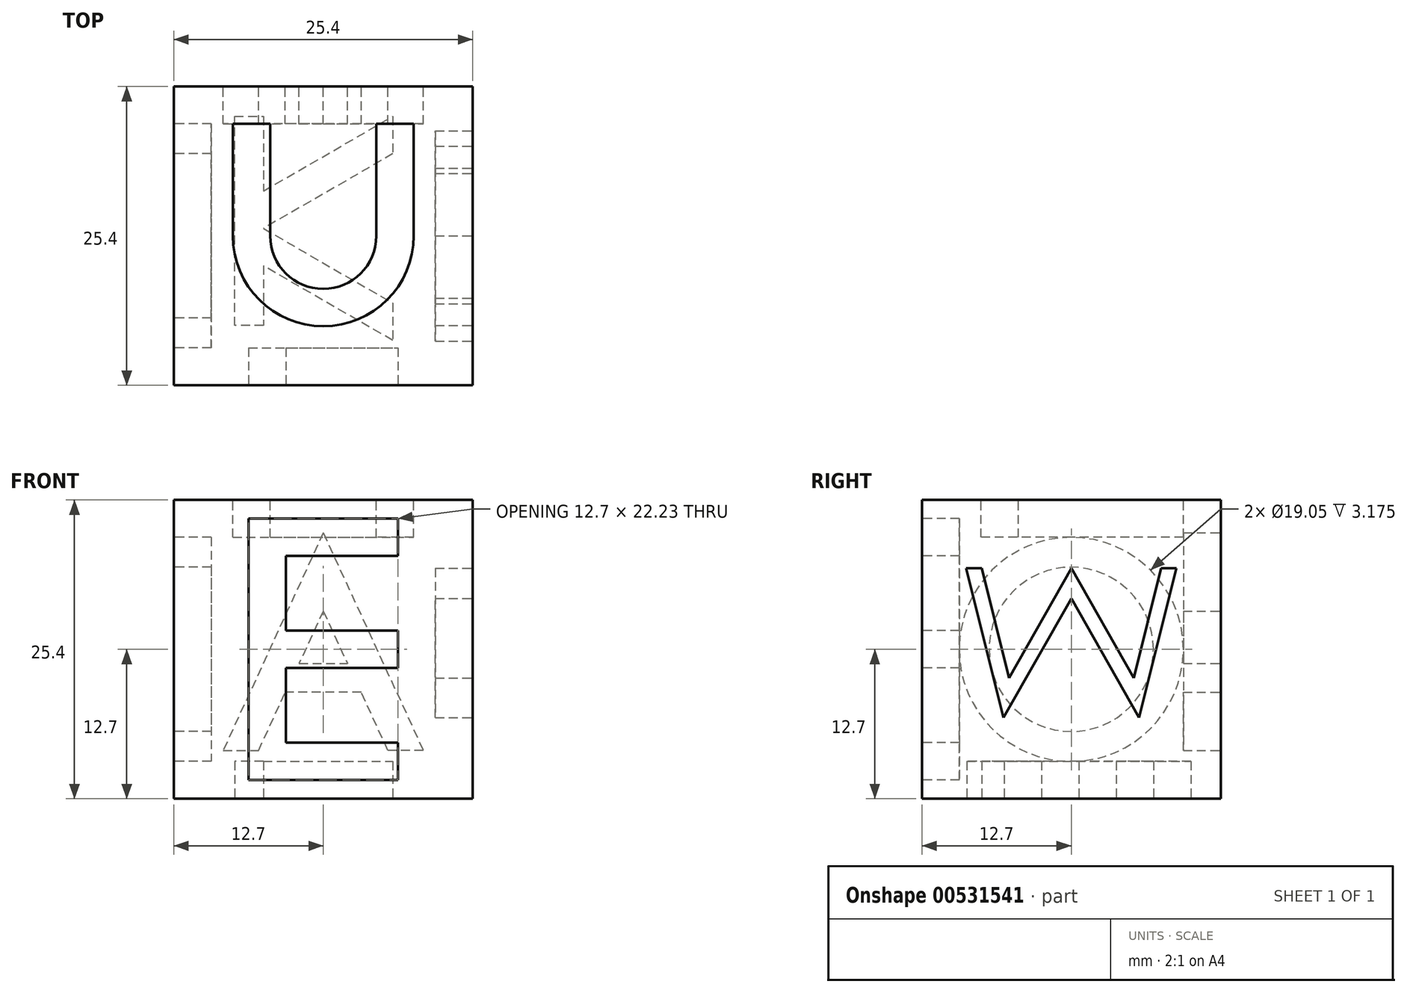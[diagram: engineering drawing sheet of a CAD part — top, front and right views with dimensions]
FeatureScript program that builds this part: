
annotation { "Feature Type Name" : "Feature", "Feature Type Description" : "" }
export const myFeature = defineFeature(function(context is Context, id is Id, definition is map)
    precondition{}
    {
        {
            var Q0;
            Q0=qCreatedBy(makeId("Top.planeOp"),FACE);
            var sketch = newSketch(context, id + "F0", { "sketchPlane" : qUnion([Q0])});
            skLineSegment(sketch, "E0.bottom", {"start": v(12.7, 12.7) * mm, "end": v(-12.7, 12.7) * mm});
            skLineSegment(sketch, "E0.top", {"start": v(12.7, -12.7) * mm, "end": v(-12.7, -12.7) * mm});
            skLineSegment(sketch, "E0.left", {"start": v(12.7, 12.7) * mm, "end": v(12.7, -12.7) * mm});
            skLineSegment(sketch, "E0.right", {"start": v(-12.7, 12.7) * mm, "end": v(-12.7, -12.7) * mm});
            skPoint(sketch, "E0.middle", {"position": v(0, 0) * mm});
            skSolve(sketch);
        }
        {
            var Q0;
            Q0=makeQuery(id+"F0.imprint","IMPRINT",FACE,{"disambiguationData":[TD([[makeQuery(id+"F0.imprint","IMPRINT",EDGE,{"derivedFrom":sQuery(id+"F0.wireOp",EDGE,"E0.bottom")}),1.0]])]});
            extrude(context, id + "F1", {"entities" : qUnion([Q0]), "depth" : 25.4 * mm, "offsetDistance" : 25.4 * mm});
        }
        {
            var Q0;
            Q0=makeQuery(id+"F1.opExtrude","SWEPT_FACE",FACE,{"disambiguationData":[OSD([sQuery(id+"F0.wireOp",EDGE,"E0.right")])]});
            var sketch = newSketch(context, id + "F2", { "sketchPlane" : qUnion([Q0])});
            skCircle(sketch, "E1", {"center": v(0, 12.7) * mm, "radius": 9.53 * mm});
            skCircle(sketch, "E2", {"center": v(0, 12.7) * mm, "radius": 6.99 * mm});
            skSolve(sketch);
        }
        {
            var Q0;
            Q0 = qSketchRegion(id + "F2", true);
            extrude(context, id + "F3", {"entities" : qUnion([Q0]), "operationType" : NewBodyOperationType.REMOVE, "oppositeDirection" : true, "depth" : 3.17 * mm, "offsetDistance" : 25.4 * mm});
        }
        {
            var Q0;
            Q0=makeQuery(id+"F1.opExtrude","SWEPT_FACE",FACE,{"disambiguationData":[OSD([sQuery(id+"F0.wireOp",EDGE,"E0.bottom")])]});
            var sketch = newSketch(context, id + "F4", { "sketchPlane" : qUnion([Q0])});
            skLineSegment(sketch, "E3", {"start": v(0, 22.61) * mm, "end": v(-8.5, 4.1) * mm});
            skPoint(sketch, "E3.startSnap0", {"position": v(0, 25.4) * mm});
            skLineSegment(sketch, "E4", {"start": v(-8.5, 4.1) * mm, "end": v(-5.5, 4.1) * mm});
            skLineSegment(sketch, "E5", {"start": v(-5.5, 4.1) * mm, "end": v(-3.23, 9.06) * mm});
            skLineSegment(sketch, "E6", {"start": v(-3.23, 9.06) * mm, "end": v(0, 9.06) * mm});
            skLineSegment(sketch, "E7", {"start": v(0, 15.96) * mm, "end": v(-2.05, 11.5) * mm});
            skLineSegment(sketch, "E8", {"start": v(-2.05, 11.5) * mm, "end": v(0, 11.5) * mm});
            skLineSegment(sketch, "E9.MirrorCS", {"start": v(0, 15.96) * mm, "end": v(2.05, 11.5) * mm});
            skLineSegment(sketch, "E10.MirrorCS", {"start": v(2.05, 11.5) * mm, "end": v(0, 11.5) * mm});
            skLineSegment(sketch, "E11.MirrorCS", {"start": v(3.23, 9.06) * mm, "end": v(0, 9.06) * mm});
            skLineSegment(sketch, "E12.MirrorCS", {"start": v(5.5, 4.1) * mm, "end": v(3.23, 9.06) * mm});
            skLineSegment(sketch, "E13.MirrorCS", {"start": v(8.5, 4.1) * mm, "end": v(5.5, 4.1) * mm});
            skLineSegment(sketch, "E14.MirrorCS", {"start": v(0, 22.61) * mm, "end": v(8.5, 4.1) * mm});
            skSolve(sketch);
        }
        {
            var Q0;
            Q0 = qSketchRegion(id + "F4", true);
            extrude(context, id + "F5", {"entities" : qUnion([Q0]), "operationType" : NewBodyOperationType.REMOVE, "oppositeDirection" : true, "depth" : 3.17 * mm, "offsetDistance" : 25.4 * mm});
        }
        {
            var Q0;
            Q0=makeQuery(id+"F1.opExtrude","SWEPT_FACE",FACE,{"disambiguationData":[OSD([sQuery(id+"F0.wireOp",EDGE,"E0.left")])]});
            var sketch = newSketch(context, id + "F6", { "sketchPlane" : qUnion([Q0])});
            skLineSegment(sketch, "E15", {"start": v(-8.93, 19.6) * mm, "end": v(-5.77, 6.9) * mm});
            skLineSegment(sketch, "E16", {"start": v(-5.77, 6.9) * mm, "end": v(0, 17.02) * mm});
            skLineSegment(sketch, "E17", {"start": v(0, 19.6) * mm, "end": v(-5.3, 10.28) * mm});
            skLineSegment(sketch, "E18", {"start": v(-5.3, 10.28) * mm, "end": v(-7.62, 19.6) * mm});
            skLineSegment(sketch, "E19", {"start": v(-7.62, 19.6) * mm, "end": v(-8.93, 19.6) * mm});
            skLineSegment(sketch, "E20.MirrorCS", {"start": v(0, 19.6) * mm, "end": v(5.3, 10.28) * mm});
            skLineSegment(sketch, "E21.MirrorCS", {"start": v(5.77, 6.9) * mm, "end": v(0, 17.02) * mm});
            skLineSegment(sketch, "E22.MirrorCS", {"start": v(5.3, 10.28) * mm, "end": v(7.62, 19.6) * mm});
            skLineSegment(sketch, "E23.MirrorCS", {"start": v(8.93, 19.6) * mm, "end": v(5.77, 6.9) * mm});
            skLineSegment(sketch, "E24.MirrorCS", {"start": v(7.62, 19.6) * mm, "end": v(8.93, 19.6) * mm});
            skSolve(sketch);
        }
        {
            var Q0;
            Q0 = qSketchRegion(id + "F6", true);
            extrude(context, id + "F7", {"entities" : qUnion([Q0]), "operationType" : NewBodyOperationType.REMOVE, "oppositeDirection" : true, "depth" : 3.17 * mm, "offsetDistance" : 25.4 * mm});
        }
        {
            var Q0;
            Q0=makeQuery(id+"F1.opExtrude","SWEPT_FACE",FACE,{"disambiguationData":[OSD([sQuery(id+"F0.wireOp",EDGE,"E0.top")])]});
            var sketch = newSketch(context, id + "F8", { "sketchPlane" : qUnion([Q0])});
            skLineSegment(sketch, "E25", {"start": v(-6.35, 23.81) * mm, "end": v(6.35, 23.81) * mm});
            skLineSegment(sketch, "E26", {"start": v(6.35, 23.81) * mm, "end": v(6.35, 20.64) * mm});
            skLineSegment(sketch, "E27", {"start": v(6.35, 20.64) * mm, "end": v(-3.18, 20.64) * mm});
            skLineSegment(sketch, "E28", {"start": v(-3.18, 20.64) * mm, "end": v(-3.17, 14.29) * mm});
            skLineSegment(sketch, "E29", {"start": v(-3.17, 14.29) * mm, "end": v(6.35, 14.29) * mm});
            skLineSegment(sketch, "E30", {"start": v(6.35, 14.29) * mm, "end": v(6.35, 11.11) * mm});
            skLineSegment(sketch, "E31", {"start": v(6.35, 11.11) * mm, "end": v(-3.17, 11.11) * mm});
            skLineSegment(sketch, "E32", {"start": v(-3.17, 11.11) * mm, "end": v(-3.17, 4.76) * mm});
            skLineSegment(sketch, "E33", {"start": v(-3.17, 4.76) * mm, "end": v(6.35, 4.76) * mm});
            skLineSegment(sketch, "E34", {"start": v(6.35, 4.76) * mm, "end": v(6.35, 1.59) * mm});
            skLineSegment(sketch, "E35", {"start": v(6.35, 1.59) * mm, "end": v(-6.35, 1.59) * mm});
            skLineSegment(sketch, "E36", {"start": v(-6.35, 1.59) * mm, "end": v(-6.35, 23.81) * mm});
            skSolve(sketch);
        }
        {
            var Q0;
            Q0 = qSketchRegion(id + "F8", true);
            extrude(context, id + "F9", {"entities" : qUnion([Q0]), "operationType" : NewBodyOperationType.REMOVE, "oppositeDirection" : true, "depth" : 3.17 * mm, "offsetDistance" : 25.4 * mm});
        }
        {
            var Q0;
            Q0=makeQuery(id+"F1.opExtrude","CAP_FACE",FACE,{"disambiguationData":[OSD([sQuery(id+"F0.wireOp",EDGE,"E0.bottom"),sQuery(id+"F0.wireOp",EDGE,"E0.top"),sQuery(id+"F0.wireOp",EDGE,"E0.left"),sQuery(id+"F0.wireOp",EDGE,"E0.right")])],"isStart":false});
            var sketch = newSketch(context, id + "F10", { "sketchPlane" : qUnion([Q0])});
            skLineSegment(sketch, "E37", {"start": v(-7.68, 9.53) * mm, "end": v(-7.68, 0) * mm});
            skArc(sketch, "E38", {"start": v(-7.68, 0) * mm, "mid": v(-5.43, -5.43) * mm, "end": v(0, -7.68) * mm});
            skArc(sketch, "E39.MirrorCS", {"start": v(7.68, 0) * mm, "mid": v(5.43, -5.43) * mm, "end": v(0, -7.68) * mm});
            skLineSegment(sketch, "E40.MirrorCS", {"start": v(7.68, 9.53) * mm, "end": v(7.68, 0) * mm});
            skLineSegment(sketch, "E41", {"start": v(-7.68, 9.53) * mm, "end": v(-4.5, 9.53) * mm});
            skLineSegment(sketch, "E42", {"start": v(-4.5, 9.53) * mm, "end": v(-4.5, 0) * mm});
            skArc(sketch, "E43", {"start": v(-4.5, 0) * mm, "mid": v(-3.19, -3.19) * mm, "end": v(0, -4.5) * mm});
            skLineSegment(sketch, "E44.MirrorCS", {"start": v(4.5, 9.53) * mm, "end": v(4.5, 0) * mm});
            skLineSegment(sketch, "E45.MirrorCS", {"start": v(7.68, 9.53) * mm, "end": v(4.5, 9.53) * mm});
            skArc(sketch, "E46.MirrorCS", {"start": v(4.5, 0) * mm, "mid": v(3.19, -3.19) * mm, "end": v(0, -4.5) * mm});
            skSolve(sketch);
        }
        {
            var Q0;
            Q0 = qSketchRegion(id + "F10", true);
            extrude(context, id + "F11", {"entities" : qUnion([Q0]), "operationType" : NewBodyOperationType.REMOVE, "oppositeDirection" : true, "depth" : 3.17 * mm, "offsetDistance" : 25.4 * mm});
        }
        {
            var Q0;
            Q0=makeQuery(id+"F1.opExtrude","CAP_FACE",FACE,{"disambiguationData":[OSD([sQuery(id+"F0.wireOp",EDGE,"E0.bottom"),sQuery(id+"F0.wireOp",EDGE,"E0.top"),sQuery(id+"F0.wireOp",EDGE,"E0.left"),sQuery(id+"F0.wireOp",EDGE,"E0.right")])],"isStart":true});
            var sketch = newSketch(context, id + "F12", { "sketchPlane" : qUnion([Q0])});
            skLineSegment(sketch, "E47", {"start": v(-7.53, 7.62) * mm, "end": v(-7.53, -10.16) * mm});
            skLineSegment(sketch, "E48", {"start": v(-7.53, -10.16) * mm, "end": v(-5.09, -10.16) * mm});
            skLineSegment(sketch, "E49", {"start": v(-5.09, -10.16) * mm, "end": v(-5.09, -3.8) * mm});
            skLineSegment(sketch, "E50", {"start": v(-5.09, -3.8) * mm, "end": v(5.91, -10.16) * mm});
            skLineSegment(sketch, "E51", {"start": v(5.91, -10.16) * mm, "end": v(5.91, -6.98) * mm});
            skLineSegment(sketch, "E52", {"start": v(5.91, -6.98) * mm, "end": v(-5.09, -0.63) * mm});
            skLineSegment(sketch, "E53", {"start": v(-5.09, -0.63) * mm, "end": v(5.91, 5.72) * mm});
            skLineSegment(sketch, "E54", {"start": v(5.91, 5.72) * mm, "end": v(5.91, 8.9) * mm});
            skLineSegment(sketch, "E55", {"start": v(5.91, 8.9) * mm, "end": v(-5.09, 2.54) * mm});
            skLineSegment(sketch, "E56", {"start": v(-5.09, 2.54) * mm, "end": v(-5.09, 7.62) * mm});
            skLineSegment(sketch, "E57", {"start": v(-5.09, 7.62) * mm, "end": v(-7.53, 7.62) * mm});
            skSolve(sketch);
        }
        {
            var Q0;
            Q0=makeQuery(id+"F12.imprint","IMPRINT",FACE,{"disambiguationData":[TD([[makeQuery(id+"F12.imprint","IMPRINT",EDGE,{"derivedFrom":sQuery(id+"F12.wireOp",EDGE,"E47")}),1.0]])]});
            extrude(context, id + "F13", {"entities" : qUnion([Q0]), "operationType" : NewBodyOperationType.REMOVE, "oppositeDirection" : true, "depth" : 3.17 * mm, "offsetDistance" : 25.4 * mm});
        }
    });
